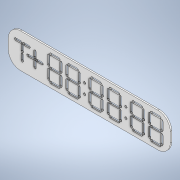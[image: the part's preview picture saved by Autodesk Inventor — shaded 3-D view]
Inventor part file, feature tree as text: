
AUTODESK INVENTOR PART (.ipt)
format: ipt  version: 2021 (Build 250183000, 183)  size: 1,112,576 bytes
history: native  units: in
note: dims shown in document units (in); Inventor stores cm internally (conversion verified against a paired STEP export)
features: other x37, extrude x2, sketch x1
ambient origin geometry x8: Origin, YZ Plane, XZ Plane, XY Plane, X Axis, Y Axis, Z Axis, Center Point
bodies: Solid1 (feature_tree)
feature tree (40):
  other  "Blocks"
  extrude  "Extrusion1"  TaperAngle=135.0deg  [1 undecoded]
  extrude  "Extrusion3"  Depth=0.8661in
  other  "Single Segment"
  other  "7 Segment Digit"
  other  "Slanted Segment Large"
  other  "+ sign"
  other  "Dot"
  other  "Clock Face with T +-"
  other  "Clock Front Face Outline"
  other  "Small Segmemt"
  sketch  "Sketch5"  dims[d10=62.9921in d11=78.7402in d29=0.1181in d30=0.0in d105=0.0866in d108=0.0866in d111=0.0866in d112=0.0866in d113=0.0866in d114=0.0866in d115=0.0866in d116=0.0394in d117=0.1969in d121=0.0866in d122=0.0866in d126=135.0deg d127=0.8661in d128=135.0deg d129=0.0984in d131=0.0433in d132=0.0433in d137=0.0433in d138=0.0433in d139=0.0433in d140=0.0433in d141=0.0433in d142=0.0433in d143=0.0433in d144=0.0433in d145=0.0433in d146=0.0433in d150=0.0433in d151=0.0433in d152=0.0433in d153=0.0433in d294=0.126in d295=0.126in d296=0.315in d297=0.126in d298=0.126in d299=2.2441in d304=0.126in d305=0.126in d306=0.126in d307=0.126in d311=0.0787in d312=0.0787in d314=0.0787in d315=0.0787in d316=0.0787in d317=0.0787in d318=0.0787in d319=0.0787in d320=0.0394in d321=0.0394in d322=0.0394in d323=0.0394in d348=0.1969in d349=0.8661in d350=0.0866in d352=0.0118in d353=0.0118in d358=0.0118in d359=0.0118in d360=0.1969in d361=0.1969in d362=0.2953in d363=0.6693in d364=0.2953in d365=0.6693in d366=0.2953in d367=0.0in d368=0.0in d369=0.0in d370=0.0in d371=0.0in d372=0.5906in d373=0.0in d374=0.6299in d375=0.2362in d376=0.2362in d377=0.5354in d378=0.6299in d379=0.2362in d380=0.5906in d381=0.0in d402=1.9528in d429=12.9921in d430=2.7559in d431=0.9843in d462=0.0866in d463=0.0866in d464=0.0866in d465=0.0866in d466=0.0866in d467=0.0866in d468=0.0866in d469=0.0394in d470=0.1969in d471=0.0866in d472=0.0866in d473=135.0deg d474=0.6299in d475=135.0deg d476=0.0984in d477=0.1969in d478=0.6299in d479=0.0866in d480=0.0118in d481=0.0118in d482=0.0118in d483=0.0118in d496=0.0787in d497=0.0787in d501=0.0394in d502=0.0394in d503=0.0in d504=0.0in d505=0.039in d506=0.039in d507=0.039in d508=0.039in d509=0.9055in d510=0.9843in d511=0.9685in d514=0.0197in d515=0.0394in d516=0.0394in d517=0.0394in d518=0.0in d519=0.039in d520=0.4331in d522=0.8268in d523=0.0in d524=0.0591in d525=0.315in d526=0.2913in d527=1.0236in d528=0.5787in d529=0.4724in d530=0.1181in d531=0.0in]
  other  "Single Segment:9"
  other  "Single Segment:10"
  other  "Single Segment:11"
  other  "Single Segment:12"
  other  "Single Segment:13"
  other  "Single Segment:14"
  other  "Single Segment:15"
  other  "7 Segment Digit:8"
  other  "7 Segment Digit:9"
  other  "7 Segment Digit:10"
  other  "7 Segment Digit:11"
  other  "7 Segment Digit:12"
  other  "7 Segment Digit:13"
  other  "Dot:7"
  other  "Dot:8"
  other  "Dot:9"
  other  "Dot:10"
  other  "Clock Front Face Outline:1"
  other  "Small Segmemt:1"
  other  "Small Segmemt:2"
  other  "Small Segmemt:3"
  other  "Small Segmemt:4"
  other  "+ sign:1"
  other  "Small Segmemt:5"
  other  "Small Segmemt:6"
  other  "Small Segmemt:7"
  other  "Small Segmemt:8"
  other  "Clock Face with T +-:1"
note: 1 required parameter value undecoded (feature->parameter linkage not recoverable at this tier; creation-order binding heuristic only, values carry confidence <= 0.55)
